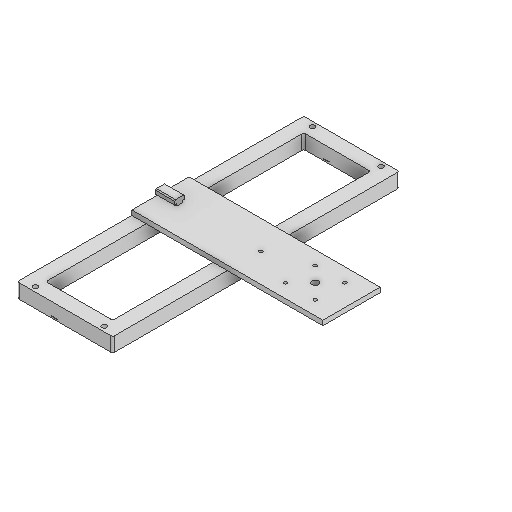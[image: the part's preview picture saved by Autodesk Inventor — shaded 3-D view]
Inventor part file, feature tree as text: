
AUTODESK INVENTOR PART (.ipt)
format: ipt  version: 2025.1 (Build 291241000, 241)  size: 217,088 bytes
history: native  units: mm
features: sketch x9, extrude x5, hole x4, other x1, fillet x1
ambient origin geometry x8: Origin, YZ Plane, XZ Plane, XY Plane, X Axis, Y Axis, Z Axis, Center Point
bodies: Body1 (feature_tree)
feature tree (20):
  other  "Bryła1"
  sketch  "Szkic1"
  sketch  "Szkic2"
  extrude  "Wyciągnięcie proste1"  Depth=300.0mm
  extrude  "Wyciągnięcie proste2"  Depth=100.0mm
  fillet  "Zaokrąglenie1"  Radius=70.0mm
  hole  "Otwór1"  [1 undecoded]
  extrude  "Wyciągnięcie proste3"  Depth=15.0mm
  extrude  "Wyciągnięcie proste4"  Depth=15.0mm
  hole  "Otwór2"  [1 undecoded]
  hole  "Otwór3"  [1 undecoded]
  hole  "Otwór4"  [1 undecoded]
  extrude  "Wyciągnięcie proste5"  Depth=5.0mm
  sketch  "Szkic3"
  sketch  "Szkic4"
  sketch  "Szkic5"
  sketch  "Szkic6"
  sketch  "Szkic7"
  sketch  "Szkic8"
  sketch  "Szkic9"
note: 4 required parameter values undecoded (feature->parameter linkage not recoverable at this tier; creation-order binding heuristic only, values carry confidence <= 0.55)
